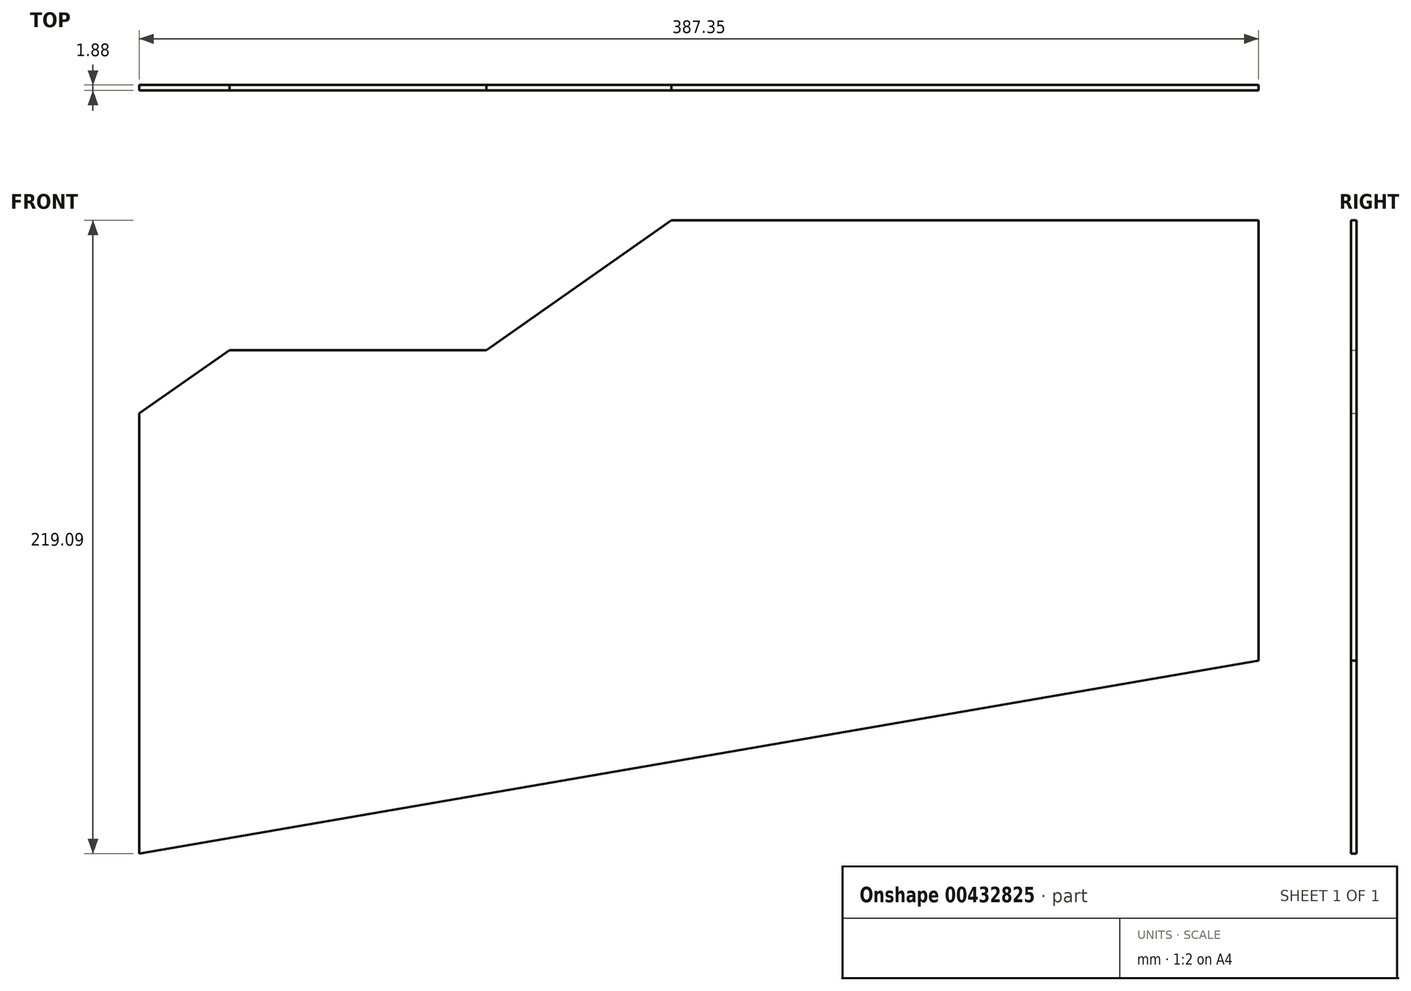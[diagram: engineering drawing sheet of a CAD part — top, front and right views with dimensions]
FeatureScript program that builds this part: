
annotation { "Feature Type Name" : "Feature", "Feature Type Description" : "" }
export const myFeature = defineFeature(function(context is Context, id is Id, definition is map)
    precondition{}
    {
        {
            var Q0;
            Q0=qCreatedBy(makeId("Front.planeOp"),FACE);
            var sketch = newSketch(context, id + "F0", { "sketchPlane" : qUnion([Q0])});
            skLineSegment(sketch, "E0", {"start": v(0, 0) * mm, "end": v(0, 152.4) * mm});
            skLineSegment(sketch, "E1", {"start": v(0, 152.4) * mm, "end": v(31.2, 174.25) * mm});
            skLineSegment(sketch, "E2", {"start": v(31.2, 174.25) * mm, "end": v(120.1, 174.25) * mm});
            skLineSegment(sketch, "E3", {"start": v(120.1, 174.25) * mm, "end": v(184.15, 219.1) * mm});
            skLineSegment(sketch, "E4", {"start": v(184.15, 219.1) * mm, "end": v(387.35, 219.1) * mm});
            skLineSegment(sketch, "E5", {"start": v(387.35, 219.1) * mm, "end": v(387.35, 66.7) * mm});
            skLineSegment(sketch, "E6", {"start": v(387.35, 66.7) * mm, "end": v(0, 0) * mm});
            skSolve(sketch);
        }
        {
            var Q0;
            Q0 = qSketchRegion(id + "F0", true);
            extrude(context, id + "F1", {"entities" : qUnion([Q0]), "depth" : 1.88 * mm});
        }
    });
